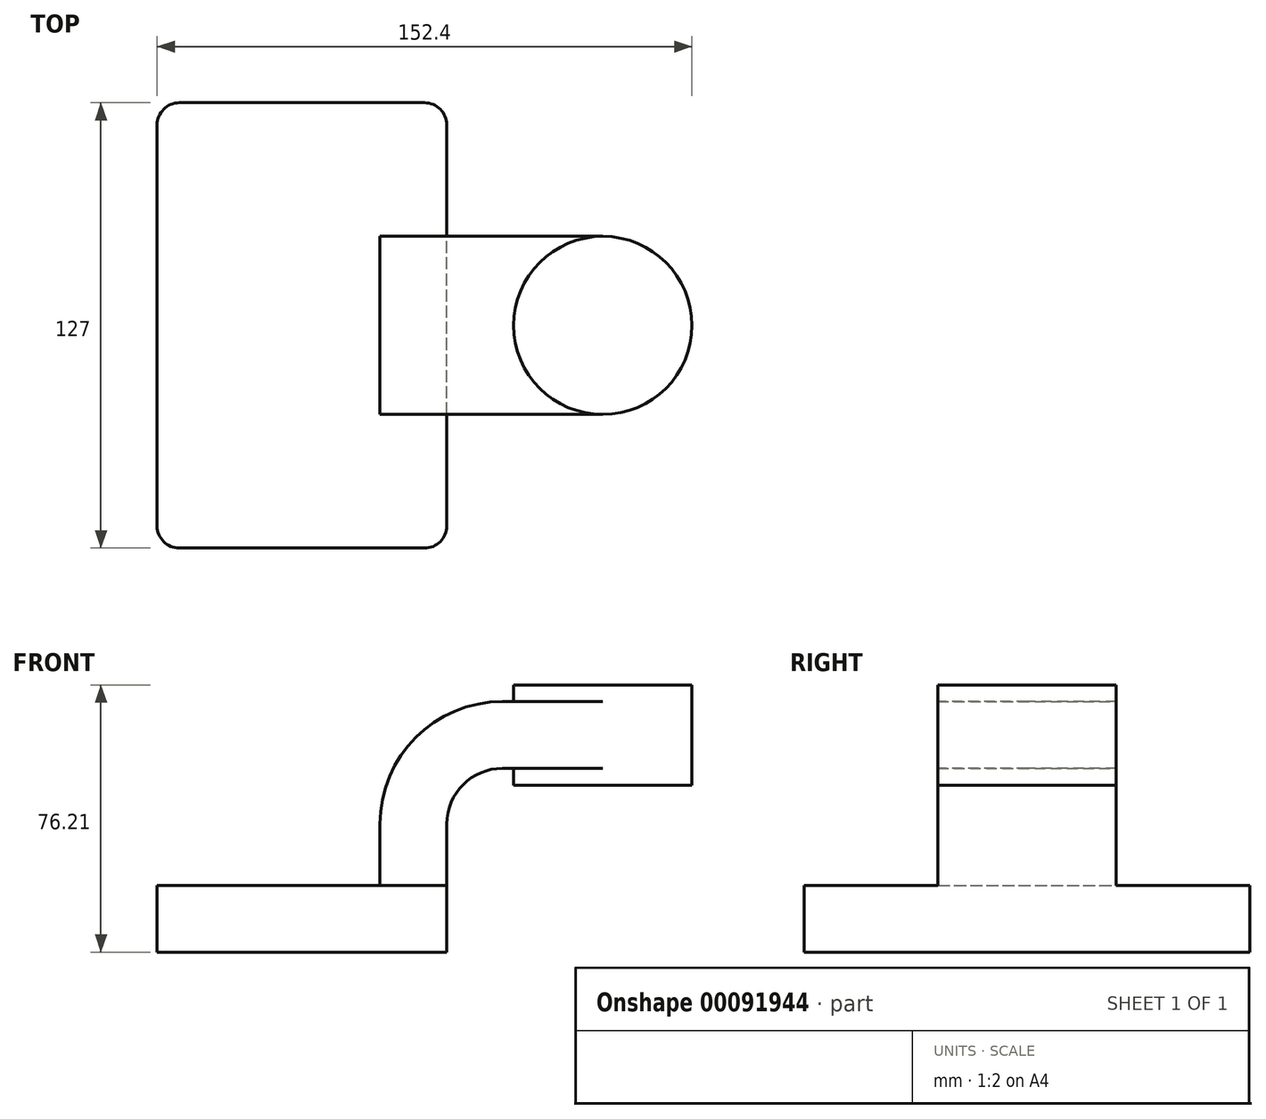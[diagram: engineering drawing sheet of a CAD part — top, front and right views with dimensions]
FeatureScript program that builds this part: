
annotation { "Feature Type Name" : "Feature", "Feature Type Description" : "" }
export const myFeature = defineFeature(function(context is Context, id is Id, definition is map)
    precondition{}
    {
        {
            var Q0;
            Q0=qCreatedBy(makeId("Front.planeOp"),FACE);
            var sketch = newSketch(context, id + "F0", { "sketchPlane" : qUnion([Q0])});
            skLineSegment(sketch, "E0.bottom", {"start": v(-41.28, 9.52) * mm, "end": v(41.28, 9.53) * mm});
            skLineSegment(sketch, "E0.top", {"start": v(-41.28, -9.53) * mm, "end": v(41.28, -9.53) * mm});
            skLineSegment(sketch, "E0.left", {"start": v(-41.28, 9.52) * mm, "end": v(-41.28, -9.53) * mm});
            skLineSegment(sketch, "E0.right", {"start": v(41.28, 9.53) * mm, "end": v(41.28, -9.52) * mm});
            skPoint(sketch, "E0.middle", {"position": v(0, 0) * mm});
            skLineSegment(sketch, "E1.bottom", {"start": v(60.32, 38.1) * mm, "end": v(111.12, 38.1) * mm});
            skLineSegment(sketch, "E1.top", {"start": v(60.32, 66.68) * mm, "end": v(111.12, 66.68) * mm});
            skLineSegment(sketch, "E1.left", {"start": v(60.32, 38.1) * mm, "end": v(60.32, 66.68) * mm});
            skLineSegment(sketch, "E1.right", {"start": v(111.12, 38.1) * mm, "end": v(111.12, 66.68) * mm});
            skPoint(sketch, "E1.middle", {"position": v(85.72, 52.39) * mm});
            skLineSegment(sketch, "E2", {"start": v(41.27, 9.53) * mm, "end": v(41.27, 27) * mm});
            skArc(sketch, "E3", {"start": v(41.27, 27) * mm, "mid": v(45.92, 38.23) * mm, "end": v(57.15, 42.88) * mm});
            skLineSegment(sketch, "E4", {"start": v(57.15, 42.88) * mm, "end": v(85.72, 42.88) * mm});
            skLineSegment(sketch, "E5.0", {"start": v(57.15, 61.93) * mm, "end": v(85.72, 61.93) * mm});
            skArc(sketch, "E5.1", {"start": v(22.22, 27) * mm, "mid": v(32.45, 51.7) * mm, "end": v(57.15, 61.93) * mm});
            skLineSegment(sketch, "E5.2", {"start": v(22.22, 9.53) * mm, "end": v(22.22, 27) * mm});
            skLineSegment(sketch, "E6", {"start": v(85.72, 38.1) * mm, "end": v(85.72, 66.68) * mm});
            skFitSpline(sketch, "E7", {"points": [v(-41.28, 9.53) * mm, v(57.15, 61.93) * mm], "startDerivative": vector(0, 98.06) * mm, "endDerivative": vector(125.3, 0) * mm});
            skSolve(sketch);
        }
        {
            var Q0;
            Q0=makeQuery(id+"F0.imprint","IMPRINT",FACE,{"disambiguationData":[TD([[makeQuery(id+"F0.imprint","IMPRINT",EDGE,{"derivedFrom":sQuery(id+"F0.wireOp",EDGE,"E0.top")}),1.0]])]});
            extrude(context, id + "F1", {"entities" : qUnion([Q0]), "endBound" : BoundingType.SYMMETRIC, "depth" : 127 * mm});
        }
        {
            var Q0;
            {var subQ1=sQuery(id+"F0.wireOp",EDGE,"E2");Q0=makeQuery(id+"F0.imprint","IMPRINT",FACE,{"disambiguationData":[TD([[makeQuery(id+"F0.imprint","IMPRINT",EDGE,{"derivedFrom":subQ1}),1.0]])]});}
            var Q1;
            {var subQ0=sQuery(id+"F0.wireOp",EDGE,"E4");var subQ1=sQuery(id+"F0.wireOp",EDGE,"E1.left");var subQ2=makeQuery(id+"F0.imprint","INTERSECT",VERTEX,{"derivedFrom":[subQ1,subQ0]});Q1=makeQuery(id+"F0.imprint","IMPRINT",FACE,{"disambiguationData":[TD([[makeQuery(id+"F0.imprint","IMPRINT",EDGE,{"disambiguationData":[TD([[subQ2,-1.0]])],"derivedFrom":subQ1}),-1.0]])]});}
            extrude(context, id + "F2", {"entities" : qUnion([Q0, Q1]), "operationType" : NewBodyOperationType.ADD, "endBound" : BoundingType.SYMMETRIC, "depth" : 50.8 * mm});
        }
        {
            var Q0;
            Q0=makeQuery(id+"F0.imprint","IMPRINT",FACE,{"disambiguationData":[TD([[makeQuery(id+"F0.imprint","IMPRINT",EDGE,{"derivedFrom":sQuery(id+"F0.wireOp",EDGE,"E5.1")}),1.0]])]});
            extrude(context, id + "F3", {"entities" : qUnion([Q0]), "operationType" : NewBodyOperationType.ADD, "endBound" : BoundingType.SYMMETRIC, "depth" : 15.88 * mm});
        }
        {
            var Q0;
            {var subQ0=sQuery(id+"F0.wireOp",EDGE,"E1.right");Q0=makeQuery(id+"F0.imprint","IMPRINT",FACE,{"disambiguationData":[TD([[makeQuery(id+"F0.imprint","IMPRINT",EDGE,{"derivedFrom":subQ0}),1.0]])]});}
            var Q1;
            Q1=sQuery(id+"F0.wireOp",EDGE,"E6");
            revolve(context, id + "F4", {"operationType" : NewBodyOperationType.ADD, "entities" : qUnion([Q0]), "axis" : qUnion([Q1]), "revolveType" : RevolveType.FULL});
        }
        {
            var Q0;
            Q0=makeQuery(id+"F1.opExtrude","CAP_EDGE",EDGE,{"disambiguationData":[OSD([sQuery(id+"F0.wireOp",EDGE,"E0.left")])],"isStart":false});
            var Q1;
            Q1=makeQuery(id+"F1.opExtrude","CAP_EDGE",EDGE,{"disambiguationData":[OSD([sQuery(id+"F0.wireOp",EDGE,"E0.right")])],"isStart":false});
            var Q2;
            Q2=makeQuery(id+"F1.opExtrude","CAP_EDGE",EDGE,{"disambiguationData":[OSD([sQuery(id+"F0.wireOp",EDGE,"E0.left")])],"isStart":true});
            var Q3;
            Q3=makeQuery(id+"F1.opExtrude","CAP_EDGE",EDGE,{"disambiguationData":[OSD([sQuery(id+"F0.wireOp",EDGE,"E0.right")])],"isStart":true});
            fillet(context, id + "F5", {"entities" : qUnion([Q0, Q1, Q2, Q3]), "radius" : 6.35 * mm, "tangentPropagation" : true, "allowEdgeOverflow" : false});
        }
    });
